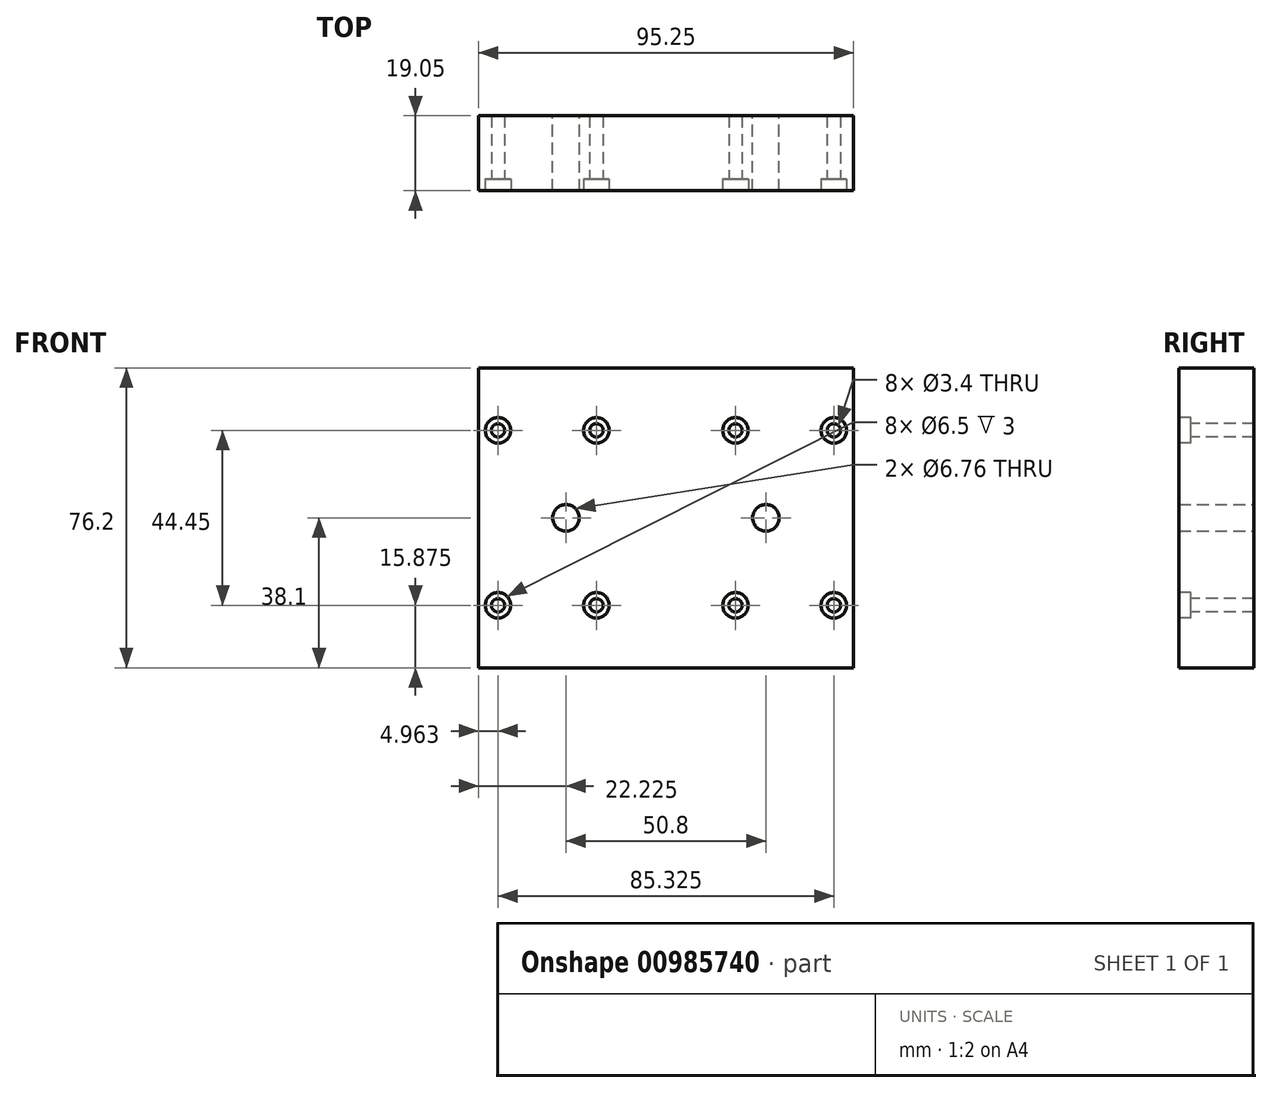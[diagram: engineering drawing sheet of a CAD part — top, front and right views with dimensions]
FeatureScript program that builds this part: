
annotation { "Feature Type Name" : "Feature", "Feature Type Description" : "" }
export const myFeature = defineFeature(function(context is Context, id is Id, definition is map)
    precondition{}
    {
        {
            var Q0;
            Q0=qCreatedBy(makeId("Front.planeOp"),FACE);
            var sketch = newSketch(context, id + "F0", { "sketchPlane" : qUnion([Q0])});
            skLineSegment(sketch, "E0.bottom", {"start": v(0, 0) * mm, "end": v(95.25, 0) * mm});
            skLineSegment(sketch, "E0.top", {"start": v(0, 76.2) * mm, "end": v(95.25, 76.2) * mm});
            skLineSegment(sketch, "E0.left", {"start": v(0, 0) * mm, "end": v(0, 76.2) * mm});
            skLineSegment(sketch, "E0.right", {"start": v(95.25, 0) * mm, "end": v(95.25, 76.2) * mm});
            skSolve(sketch);
        }
        {
            var Q0;
            Q0 = qSketchRegion(id + "F0", true);
            extrude(context, id + "F1", {"entities" : qUnion([Q0]), "depth" : 19.05 * mm, "offsetDistance" : 25.4 * mm});
        }
        {
            var Q0;
            Q0=makeQuery(id+"F1.opExtrude","CAP_FACE",FACE,{"disambiguationData":[OSD([sQuery(id+"F0.wireOp",EDGE,"E0.bottom"),sQuery(id+"F0.wireOp",EDGE,"E0.top"),sQuery(id+"F0.wireOp",EDGE,"E0.left"),sQuery(id+"F0.wireOp",EDGE,"E0.right")])],"isStart":false});
            var sketch = newSketch(context, id + "F2", { "sketchPlane" : qUnion([Q0])});
            skLineSegment(sketch, "E1", {"start": v(4.96, 60.32) * mm, "end": v(29.96, 60.32) * mm, "construction": true});
            skLineSegment(sketch, "E2", {"start": v(29.96, 60.32) * mm, "end": v(65.29, 60.32) * mm, "construction": true});
            skLineSegment(sketch, "E3", {"start": v(65.29, 60.32) * mm, "end": v(90.29, 60.32) * mm, "construction": true});
            skLineSegment(sketch, "E4", {"start": v(90.29, 60.32) * mm, "end": v(90.29, 15.88) * mm, "construction": true});
            skLineSegment(sketch, "E5", {"start": v(90.29, 15.88) * mm, "end": v(65.29, 15.88) * mm, "construction": true});
            skLineSegment(sketch, "E6", {"start": v(65.29, 15.88) * mm, "end": v(29.96, 15.88) * mm, "construction": true});
            skLineSegment(sketch, "E7", {"start": v(29.96, 15.88) * mm, "end": v(4.96, 15.87) * mm, "construction": true});
            skLineSegment(sketch, "E8", {"start": v(4.96, 15.88) * mm, "end": v(4.96, 60.32) * mm, "construction": true});
            skLineSegment(sketch, "E9", {"start": v(4.96, 38.1) * mm, "end": v(0, 38.1) * mm, "construction": true});
            skLineSegment(sketch, "E10", {"start": v(47.62, 60.32) * mm, "end": v(47.62, 76.2) * mm, "construction": true});
            skLineSegment(sketch, "E11", {"start": v(17.46, 60.32) * mm, "end": v(17.46, 15.88) * mm, "construction": true});
            skPoint(sketch, "E12", {"position": v(4.96, 60.32) * mm});
            skPoint(sketch, "E13", {"position": v(29.96, 60.32) * mm});
            skPoint(sketch, "E14", {"position": v(65.29, 60.32) * mm});
            skPoint(sketch, "E15", {"position": v(90.29, 60.32) * mm});
            skPoint(sketch, "E16", {"position": v(90.29, 15.88) * mm});
            skPoint(sketch, "E17", {"position": v(65.29, 15.88) * mm});
            skPoint(sketch, "E18", {"position": v(29.96, 15.88) * mm});
            skPoint(sketch, "E19", {"position": v(4.96, 15.88) * mm});
            skLineSegment(sketch, "E20", {"start": v(77.79, 60.32) * mm, "end": v(77.79, 15.88) * mm, "construction": true});
            skSolve(sketch);
        }
        {
            var Q0;
            Q0=sQuery(id+"F2.wireOp",VERTEX,"E12");
            var Q1;
            Q1=sQuery(id+"F2.wireOp",VERTEX,"E13");
            var Q2;
            Q2=sQuery(id+"F2.wireOp",VERTEX,"E14");
            var Q3;
            Q3=sQuery(id+"F2.wireOp",VERTEX,"E15");
            var Q4;
            Q4=sQuery(id+"F2.wireOp",VERTEX,"E19");
            var Q5;
            Q5=sQuery(id+"F2.wireOp",VERTEX,"E18");
            var Q6;
            Q6=sQuery(id+"F2.wireOp",VERTEX,"E17");
            var Q7;
            Q7=sQuery(id+"F2.wireOp",VERTEX,"E16");
            var Q8;
            Q8=makeQuery(id+"F1.opExtrude","SWEPT_BODY",BODY,{"disambiguationData":[OSD([sQuery(id+"F0.wireOp",EDGE,"E0.bottom"),sQuery(id+"F0.wireOp",EDGE,"E0.top"),sQuery(id+"F0.wireOp",EDGE,"E0.left"),sQuery(id+"F0.wireOp",EDGE,"E0.right")])]});
            hole(context, id + "F3", {"style" : HoleStyle.C_BORE, "endStyle" : HoleEndStyle.THROUGH, "standardTappedOrClearance" : lookupTablePath({ "fit" : "Normal", "standard" : "ISO", "size" : "M3", "type" : "Clearance" }), "standardBlindInLast" : lookupTablePath({ "fit" : "Normal", "standard" : "ISO", "engagement" : "75%", "pitch" : "0.5 mm", "size" : "M3", "type" : "Clearance & tapped" }), "holeDiameter" : 3.4 * mm, "cBoreDiameter" : 6.5 * mm, "cBoreDepth" : 3 * mm, "majorDiameter" : 3 * mm, "isTappedThrough" : true, "tappedDepth" : 19.05 * mm, "tapClearance" : 3, "startFromSketch" : true, "locations" : qUnion([Q0, Q1, Q2, Q3, Q4, Q5, Q6, Q7]), "scope" : qUnion([Q8])});
        }
        {
            var Q0;
            Q0=makeQuery(id+"F1.opExtrude","CAP_FACE",FACE,{"disambiguationData":[OSD([sQuery(id+"F0.wireOp",EDGE,"E0.bottom"),sQuery(id+"F0.wireOp",EDGE,"E0.top"),sQuery(id+"F0.wireOp",EDGE,"E0.left"),sQuery(id+"F0.wireOp",EDGE,"E0.right")])],"isStart":true});
            var sketch = newSketch(context, id + "F4", { "sketchPlane" : qUnion([Q0])});
            skLineSegment(sketch, "E21", {"start": v(-73.03, 38.1) * mm, "end": v(-22.23, 38.1) * mm, "construction": true});
            skLineSegment(sketch, "E22", {"start": v(-47.63, 38.1) * mm, "end": v(-47.63, 0) * mm, "construction": true});
            skSolve(sketch);
        }
        {
            var Q0;
            Q0=sQuery(id+"F4.wireOp",VERTEX,"E21.start");
            var Q1;
            Q1=sQuery(id+"F4.wireOp",VERTEX,"E21.end");
            var Q2;
            Q2=makeQuery(id+"F1.opExtrude","SWEPT_BODY",BODY,{"disambiguationData":[OSD([sQuery(id+"F0.wireOp",EDGE,"E0.bottom"),sQuery(id+"F0.wireOp",EDGE,"E0.top"),sQuery(id+"F0.wireOp",EDGE,"E0.left"),sQuery(id+"F0.wireOp",EDGE,"E0.right")])]});
            hole(context, id + "F5", {"style" : HoleStyle.SIMPLE, "endStyle" : HoleEndStyle.THROUGH, "standardTappedOrClearance" : lookupTablePath({ "fit" : "Free", "standard" : "ANSI", "size" : "1/4", "type" : "Clearance" }), "standardBlindInLast" : lookupTablePath({ "fit" : "Free", "standard" : "ANSI", "engagement" : "75%", "pitch" : "20 tpi", "size" : "1/4", "type" : "Clearance & tapped" }), "holeDiameter" : 6.76 * mm, "majorDiameter" : 6.35 * mm, "isTappedThrough" : true, "tappedDepth" : 19.05 * mm, "tapClearance" : 3, "startFromSketch" : true, "locations" : qUnion([Q0, Q1]), "scope" : qUnion([Q2])});
        }
    });
